# Revit family: CL 52 Pusher feed-head 1 speed (a)
name_source: partatom
category: Equipement spécialisé
revit_build: Autodesk Revit LT 2015 (Build: 20140606_1530(x64)
units: mm (PartAtom-declared; Revit-internal decimal feet)

## types (8) — shared parameters
Apparent Power = 0 VA
Description = COUPE-LEGUMES
Electrique connexion = 133 mm
Fabricant = ROBOT COUPE
Height = 684 mm  [stored 2.24409 ft]
UP Delpth = 618 mm
UP Height = 868 mm
URL = www.robot-coupe.com
water = Connector
zero-valued in all types: Cold water supply, Cold water supply height, Top, Used water, Waste water height

## per-type parameters (varying)
| type | Amps | Cycle | Depth | HP | Modèle | Phase | Speeds (Rpm) | Volts | Watts | Weight | Width |
| CL52 Pusher feed-head 1 speed  230/50/1 | 5.3 A | 50 Hz | 370 mm |  | CL52 Pusher feed-head 1 speed | 1 | 375 | 230 V | 750 W | 28 Kg | 327 mm |
| CL52 Pusher feed-head 1 speed  120/60/1 | 8.9 A | 60 Hz | 323 mm |  | CL52 Pusher feed-head 1 speed | 1 | 375 | 120 V | 750 W | 28 Kg | 370 mm |
| CL52 Pusher feed-head 1 speed  220/60/1 | 5.3 A | 60 Hz | 370 mm |  | CL52 Pusher feed-head 1 speed | 1 | 375 | 220 V | 750 W | 28 Kg | 327 mm |
| CL52 Pusher feed-head 1 speed  220-240/50/1 | 5.3 A | 50 Hz | 370 mm |  | CL52 Pusher feed-head 1 speed | 1 | 375 | 240 V | 750 W | 28 Kg | 327 mm |
| CL52 Pusher feed-head 1 speed  400/50/3 | 2 A | 50 Hz | 370 mm |  | CL52 Pusher feed-head 1 speed | 3 | 375 | 400 V | 750 W | 28 Kg | 327 mm |
| CL52 Pusher feed-head 1 speed  220/60/3 | 4.4 A | 60 Hz | 370 mm |  | CL52 Pusher feed-head 1 speed | 3 | 375 | 220 V | 750 W | 28 Kg | 327 mm |
| CL52 Pusher feed-head 1 speed  380/60/3 | 2.6 A | 60 Hz | 370 mm |  | CL52 Pusher feed-head 1 speed | 3 | 375 | 380 V | 750 W | 28 Kg | 327 mm |
| CL52 Pusher feed-head USA 1 speed  120/60/1 | 13.5 A | 60 Hz | 323 mm | 2 | CL52 Pusher feed-head USA 1 speed | 1 | 425 | 120 V | 0 W | 62 lbs | 370 mm |

note: [stored X ft] marks values corroborated as IEEE doubles in the binary element streams (Revit-internal decimal feet)

## geometry (parser evidence)
native form markers: Blend x102, Sweep x4
no freeform markers — native parametric forms only
